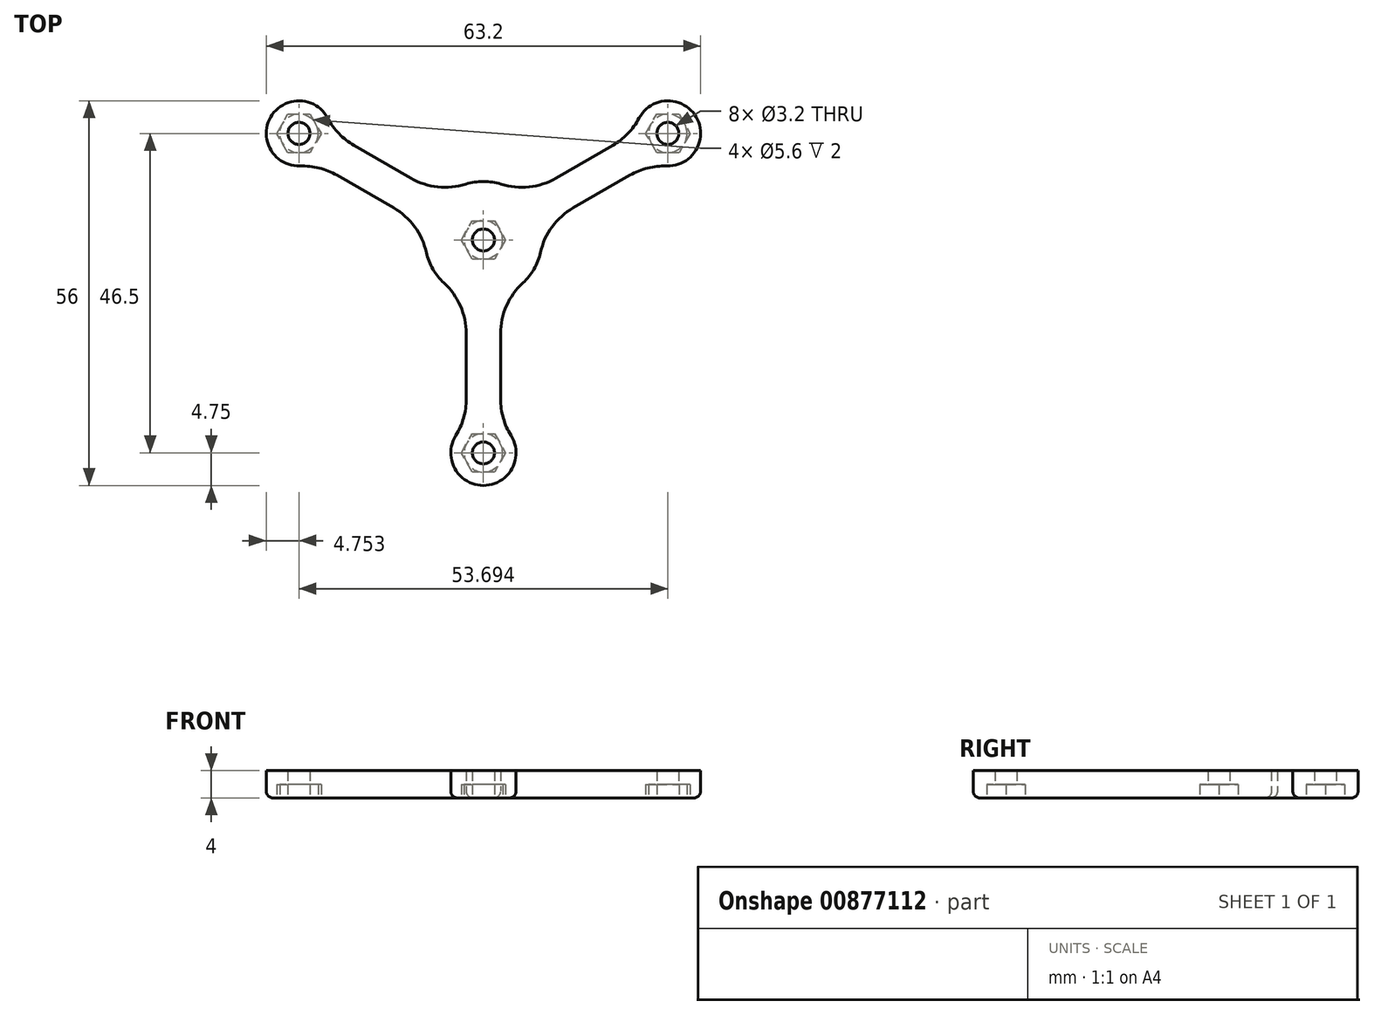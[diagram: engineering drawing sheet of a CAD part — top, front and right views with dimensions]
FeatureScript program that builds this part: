
annotation { "Feature Type Name" : "Feature", "Feature Type Description" : "" }
export const myFeature = defineFeature(function(context is Context, id is Id, definition is map)
    precondition{}
    {
        {
            var Q0;
            Q0=qCreatedBy(makeId("Top.planeOp"),FACE);
            var sketch = newSketch(context, id + "F0", { "sketchPlane" : qUnion([Q0])});
            skPoint(sketch, "E0.center", {"position": v(0, 0) * mm});
            skCircle(sketch, "E1", {"center": v(0, -31) * mm, "radius": 1.6 * mm});
            skCircle(sketch, "E2.cCircle", {"center": v(0, -31) * mm, "radius": 2.8 * mm});
            skLineSegment(sketch, "E2.0", {"start": v(3.23, -31) * mm, "end": v(1.62, -33.8) * mm});
            skLineSegment(sketch, "E2.1", {"start": v(1.62, -33.8) * mm, "end": v(-1.62, -33.8) * mm});
            skLineSegment(sketch, "E2.2", {"start": v(-1.62, -33.8) * mm, "end": v(-3.23, -31) * mm});
            skLineSegment(sketch, "E2.3", {"start": v(-3.23, -31) * mm, "end": v(-1.62, -28.2) * mm});
            skLineSegment(sketch, "E2.4", {"start": v(-1.62, -28.2) * mm, "end": v(1.62, -28.2) * mm});
            skLineSegment(sketch, "E2.5", {"start": v(1.62, -28.2) * mm, "end": v(3.23, -31) * mm});
            skPoint(sketch, "E2.0.midPoint", {"position": v(2.42, -32.4) * mm});
            skPoint(sketch, "E3.0.1.1", {"position": v(2.42, -1.4) * mm});
            skLineSegment(sketch, "E3.0.1.2", {"start": v(-1.62, -2.8) * mm, "end": v(-3.23, 0) * mm});
            skCircle(sketch, "E3.0.1.3", {"center": v(0, 0) * mm, "radius": 2.8 * mm});
            skLineSegment(sketch, "E3.0.1.4", {"start": v(1.62, -2.8) * mm, "end": v(-1.62, -2.8) * mm});
            skLineSegment(sketch, "E3.0.1.5", {"start": v(-1.62, 2.8) * mm, "end": v(1.62, 2.8) * mm});
            skLineSegment(sketch, "E3.0.1.6", {"start": v(3.23, 0) * mm, "end": v(1.62, -2.8) * mm});
            skLineSegment(sketch, "E3.0.1.7", {"start": v(1.62, 2.8) * mm, "end": v(3.23, 0) * mm});
            skLineSegment(sketch, "E3.0.1.8", {"start": v(-3.23, 0) * mm, "end": v(-1.62, 2.8) * mm});
            skCircle(sketch, "E3.0.1.9", {"center": v(0, 0) * mm, "radius": 1.6 * mm});
            skLineSegment(sketch, "E3.direction1", {"start": v(-1.62, -33.8) * mm, "end": v(2.23, -33.8) * mm, "construction": true});
            skLineSegment(sketch, "E3.direction2", {"start": v(-1.62, -33.8) * mm, "end": v(-1.62, -2.8) * mm, "construction": true});
            skLineSegment(sketch, "E4", {"start": v(-2.5, -8.12) * mm, "end": v(-2.5, -8.12) * mm});
            skLineSegment(sketch, "E5", {"start": v(2.5, -13.64) * mm, "end": v(2.5, -23.17) * mm});
            skArc(sketch, "E6", {"start": v(-5.79, 6.23) * mm, "mid": v(-5.84, 6.18) * mm, "end": v(-5.9, 6.13) * mm});
            skArc(sketch, "E7", {"start": v(-4.03, -28.48) * mm, "mid": v(0, -35.75) * mm, "end": v(4.03, -28.48) * mm});
            skLineSegment(sketch, "E8", {"start": v(-2.5, -13.64) * mm, "end": v(-2.5, -23.17) * mm});
            skArc(sketch, "E9", {"start": v(-8.3, -1.84) * mm, "mid": v(-7.36, -4.25) * mm, "end": v(-5.74, -6.27) * mm});
            skPoint(sketch, "E10.visualSharp", {"position": v(-2.5, -26.96) * mm});
            skArc(sketch, "E10.filletArc", {"start": v(-4.03, -28.48) * mm, "mid": v(-2.89, -25.93) * mm, "end": v(-2.5, -23.17) * mm});
            skPoint(sketch, "E11.visualSharp", {"position": v(2.5, -26.96) * mm});
            skArc(sketch, "E11.filletArc", {"start": v(2.5, -23.17) * mm, "mid": v(2.89, -25.93) * mm, "end": v(4.03, -28.48) * mm});
            skLineSegment(sketch, "E12.1.0", {"start": v(10.56, 8.98) * mm, "end": v(18.82, 13.75) * mm});
            skPoint(sketch, "E12.1.1", {"position": v(26.85, 18.3) * mm});
            skLineSegment(sketch, "E12.1.2", {"start": v(13.06, 4.65) * mm, "end": v(21.32, 9.42) * mm});
            skPoint(sketch, "E12.1.3", {"position": v(22.1, 15.65) * mm});
            skArc(sketch, "E12.1.4", {"start": v(26.68, 10.75) * mm, "mid": v(23.9, 10.46) * mm, "end": v(21.32, 9.42) * mm});
            skCircle(sketch, "E12.1.5", {"center": v(26.85, 15.5) * mm, "radius": 2.8 * mm});
            skCircle(sketch, "E12.1.6", {"center": v(26.85, 15.5) * mm, "radius": 1.6 * mm});
            skArc(sketch, "E12.1.7", {"start": v(26.68, 10.75) * mm, "mid": v(30.96, 17.87) * mm, "end": v(22.65, 17.73) * mm});
            skArc(sketch, "E12.1.8", {"start": v(18.82, 13.75) * mm, "mid": v(21.01, 15.47) * mm, "end": v(22.65, 17.73) * mm});
            skPoint(sketch, "E12.1.9", {"position": v(24.6, 11.32) * mm});
            skLineSegment(sketch, "E12.1.10", {"start": v(25.23, 12.7) * mm, "end": v(23.61, 15.5) * mm});
            skLineSegment(sketch, "E12.1.11", {"start": v(30.08, 15.5) * mm, "end": v(28.46, 12.7) * mm});
            skLineSegment(sketch, "E12.1.12", {"start": v(28.46, 12.7) * mm, "end": v(25.23, 12.7) * mm});
            skLineSegment(sketch, "E12.1.13", {"start": v(23.61, 15.5) * mm, "end": v(25.23, 18.3) * mm});
            skLineSegment(sketch, "E12.1.14", {"start": v(25.23, 18.3) * mm, "end": v(28.46, 18.3) * mm});
            skLineSegment(sketch, "E12.1.15", {"start": v(28.46, 18.3) * mm, "end": v(30.08, 15.5) * mm});
            skLineSegment(sketch, "E12.2.0", {"start": v(-13.06, 4.65) * mm, "end": v(-21.32, 9.42) * mm});
            skPoint(sketch, "E12.2.1", {"position": v(-29.27, 14.1) * mm});
            skLineSegment(sketch, "E12.2.2", {"start": v(-10.56, 8.98) * mm, "end": v(-18.82, 13.75) * mm});
            skPoint(sketch, "E12.2.3", {"position": v(-24.6, 11.32) * mm});
            skArc(sketch, "E12.2.4", {"start": v(-22.65, 17.73) * mm, "mid": v(-21.01, 15.47) * mm, "end": v(-18.82, 13.75) * mm});
            skCircle(sketch, "E12.2.5", {"center": v(-26.85, 15.5) * mm, "radius": 2.8 * mm});
            skCircle(sketch, "E12.2.6", {"center": v(-26.85, 15.5) * mm, "radius": 1.6 * mm});
            skArc(sketch, "E12.2.7", {"start": v(-22.65, 17.73) * mm, "mid": v(-30.96, 17.87) * mm, "end": v(-26.68, 10.75) * mm});
            skArc(sketch, "E12.2.8", {"start": v(-21.32, 9.42) * mm, "mid": v(-23.9, 10.46) * mm, "end": v(-26.68, 10.75) * mm});
            skPoint(sketch, "E12.2.9", {"position": v(-22.1, 15.65) * mm});
            skLineSegment(sketch, "E12.2.10", {"start": v(-23.61, 15.5) * mm, "end": v(-25.23, 12.7) * mm});
            skLineSegment(sketch, "E12.2.11", {"start": v(-28.46, 18.3) * mm, "end": v(-25.23, 18.3) * mm});
            skLineSegment(sketch, "E12.2.12", {"start": v(-25.23, 18.3) * mm, "end": v(-23.61, 15.5) * mm});
            skLineSegment(sketch, "E12.2.13", {"start": v(-25.23, 12.7) * mm, "end": v(-28.46, 12.7) * mm});
            skLineSegment(sketch, "E12.2.14", {"start": v(-28.46, 12.7) * mm, "end": v(-30.08, 15.5) * mm});
            skLineSegment(sketch, "E12.2.15", {"start": v(-30.08, 15.5) * mm, "end": v(-28.46, 18.3) * mm});
            skArc(sketch, "E13.trimOffspring", {"start": v(2.56, 8.1) * mm, "mid": v(0, 8.5) * mm, "end": v(-2.56, 8.1) * mm});
            skArc(sketch, "E14.trimOffspring", {"start": v(5.74, -6.27) * mm, "mid": v(7.36, -4.25) * mm, "end": v(8.3, -1.84) * mm});
            skPoint(sketch, "E15.visualSharp", {"position": v(-5.79, 6.23) * mm});
            skArc(sketch, "E15.filletArc", {"start": v(-10.56, 8.98) * mm, "mid": v(-6.65, 7.7) * mm, "end": v(-2.56, 8.1) * mm});
            skPoint(sketch, "E16.visualSharp", {"position": v(5.79, 6.23) * mm});
            skArc(sketch, "E16.filletArc", {"start": v(2.56, 8.1) * mm, "mid": v(6.65, 7.7) * mm, "end": v(10.56, 8.98) * mm});
            skPoint(sketch, "E17.visualSharp", {"position": v(8.29, 1.9) * mm});
            skArc(sketch, "E17.filletArc", {"start": v(13.06, 4.65) * mm, "mid": v(10, 1.9) * mm, "end": v(8.3, -1.84) * mm});
            skPoint(sketch, "E18.visualSharp", {"position": v(-8.29, 1.9) * mm});
            skArc(sketch, "E18.filletArc", {"start": v(-8.3, -1.84) * mm, "mid": v(-10, 1.9) * mm, "end": v(-13.06, 4.65) * mm});
            skPoint(sketch, "E19.visualSharp", {"position": v(-2.5, -8.12) * mm});
            skArc(sketch, "E19.filletArc", {"start": v(-2.5, -13.64) * mm, "mid": v(-3.35, -9.61) * mm, "end": v(-5.74, -6.27) * mm});
            skPoint(sketch, "E20.visualSharp", {"position": v(2.5, -8.12) * mm});
            skArc(sketch, "E20.filletArc", {"start": v(5.74, -6.27) * mm, "mid": v(3.35, -9.61) * mm, "end": v(2.5, -13.64) * mm});
            skCircle(sketch, "E21", {"center": v(-26.85, 15.5) * mm, "radius": 17 * mm, "construction": true});
            skCircle(sketch, "E22", {"center": v(26.85, 15.5) * mm, "radius": 17 * mm, "construction": true});
            skCircle(sketch, "E23", {"center": v(0, 0) * mm, "radius": 17 * mm, "construction": true});
            skCircle(sketch, "E24", {"center": v(0, -31) * mm, "radius": 17 * mm, "construction": true});
            skSolve(sketch);
        }
        {
            var Q0;
            {var subQ0=sQuery(id+"F0.wireOp",EDGE,"E12.2.11");var subQ1=sQuery(id+"F0.wireOp",EDGE,"E12.2.5");var subQ2=makeQuery(id+"F0.imprint","INTERSECT",VERTEX,{"derivedFrom":[subQ1,subQ0]});Q0=makeQuery(id+"F0.imprint","IMPRINT",FACE,{"disambiguationData":[TD([[makeQuery(id+"F0.imprint","IMPRINT",EDGE,{"disambiguationData":[TD([[subQ2,-1.0]])],"derivedFrom":subQ1}),-1.0]])]});}
            var Q1;
            {var subQ0=sQuery(id+"F0.wireOp",EDGE,"E12.2.15");var subQ1=sQuery(id+"F0.wireOp",EDGE,"E12.2.5");var subQ2=makeQuery(id+"F0.imprint","INTERSECT",VERTEX,{"derivedFrom":[subQ1,subQ0]});Q1=makeQuery(id+"F0.imprint","IMPRINT",FACE,{"disambiguationData":[TD([[makeQuery(id+"F0.imprint","IMPRINT",EDGE,{"disambiguationData":[TD([[subQ2,-1.0]])],"derivedFrom":subQ1}),-1.0]])]});}
            var Q2;
            {var subQ0=sQuery(id+"F0.wireOp",EDGE,"E12.2.13");var subQ1=sQuery(id+"F0.wireOp",EDGE,"E12.2.5");var subQ2=makeQuery(id+"F0.imprint","INTERSECT",VERTEX,{"derivedFrom":[subQ1,subQ0]});Q2=makeQuery(id+"F0.imprint","IMPRINT",FACE,{"disambiguationData":[TD([[makeQuery(id+"F0.imprint","IMPRINT",EDGE,{"disambiguationData":[TD([[subQ2,1.0]])],"derivedFrom":subQ1}),-1.0]])]});}
            var Q3;
            Q3=makeQuery(id+"F0.imprint","IMPRINT",FACE,{"disambiguationData":[TD([[makeQuery(id+"F0.imprint","IMPRINT",EDGE,{"derivedFrom":sQuery(id+"F0.wireOp",EDGE,"E12.2.6")}),-1.0]])]});
            var Q4;
            {var subQ0=sQuery(id+"F0.wireOp",EDGE,"E12.2.12");var subQ1=sQuery(id+"F0.wireOp",EDGE,"E12.2.5");var subQ2=makeQuery(id+"F0.imprint","INTERSECT",VERTEX,{"derivedFrom":[subQ1,subQ0]});Q4=makeQuery(id+"F0.imprint","IMPRINT",FACE,{"disambiguationData":[TD([[makeQuery(id+"F0.imprint","IMPRINT",EDGE,{"disambiguationData":[TD([[subQ2,-1.0]])],"derivedFrom":subQ1}),-1.0]])]});}
            var Q5;
            {var subQ0=sQuery(id+"F0.wireOp",EDGE,"E12.2.10");var subQ1=sQuery(id+"F0.wireOp",EDGE,"E12.2.5");var subQ2=makeQuery(id+"F0.imprint","INTERSECT",VERTEX,{"derivedFrom":[subQ1,subQ0]});Q5=makeQuery(id+"F0.imprint","IMPRINT",FACE,{"disambiguationData":[TD([[makeQuery(id+"F0.imprint","IMPRINT",EDGE,{"disambiguationData":[TD([[subQ2,-1.0]])],"derivedFrom":subQ1}),-1.0]])]});}
            var Q6;
            {var subQ0=sQuery(id+"F0.wireOp",EDGE,"E12.2.10");var subQ1=sQuery(id+"F0.wireOp",EDGE,"E12.2.5");var subQ2=makeQuery(id+"F0.imprint","INTERSECT",VERTEX,{"derivedFrom":[subQ1,subQ0]});Q6=makeQuery(id+"F0.imprint","IMPRINT",FACE,{"disambiguationData":[TD([[makeQuery(id+"F0.imprint","IMPRINT",EDGE,{"disambiguationData":[TD([[subQ2,1.0]])],"derivedFrom":subQ1}),-1.0]])]});}
            var Q7;
            {var subQ0=sQuery(id+"F0.wireOp",EDGE,"E3.0.1.5");var subQ1=sQuery(id+"F0.wireOp",EDGE,"E3.0.1.3");var subQ2=makeQuery(id+"F0.imprint","INTERSECT",VERTEX,{"derivedFrom":[subQ1,subQ0]});Q7=makeQuery(id+"F0.imprint","IMPRINT",FACE,{"disambiguationData":[TD([[makeQuery(id+"F0.imprint","IMPRINT",EDGE,{"disambiguationData":[TD([[subQ2,-1.0]])],"derivedFrom":subQ1}),-1.0]])]});}
            var Q8;
            Q8=makeQuery(id+"F0.imprint","IMPRINT",FACE,{"disambiguationData":[TD([[makeQuery(id+"F0.imprint","IMPRINT",EDGE,{"derivedFrom":sQuery(id+"F0.wireOp",EDGE,"E3.0.1.9")}),-1.0]])]});
            var Q9;
            {var subQ0=sQuery(id+"F0.wireOp",EDGE,"E3.0.1.5");var subQ1=sQuery(id+"F0.wireOp",EDGE,"E3.0.1.3");var subQ2=makeQuery(id+"F0.imprint","INTERSECT",VERTEX,{"derivedFrom":[subQ1,subQ0]});Q9=makeQuery(id+"F0.imprint","IMPRINT",FACE,{"disambiguationData":[TD([[makeQuery(id+"F0.imprint","IMPRINT",EDGE,{"disambiguationData":[TD([[subQ2,1.0]])],"derivedFrom":subQ1}),-1.0]])]});}
            var Q10;
            {var subQ0=sQuery(id+"F0.wireOp",EDGE,"E3.0.1.7");var subQ1=sQuery(id+"F0.wireOp",EDGE,"E3.0.1.3");var subQ2=makeQuery(id+"F0.imprint","INTERSECT",VERTEX,{"derivedFrom":[subQ1,subQ0]});Q10=makeQuery(id+"F0.imprint","IMPRINT",FACE,{"disambiguationData":[TD([[makeQuery(id+"F0.imprint","IMPRINT",EDGE,{"disambiguationData":[TD([[subQ2,1.0]])],"derivedFrom":subQ1}),-1.0]])]});}
            var Q11;
            {var subQ0=sQuery(id+"F0.wireOp",EDGE,"E3.0.1.4");var subQ1=sQuery(id+"F0.wireOp",EDGE,"E3.0.1.3");var subQ2=makeQuery(id+"F0.imprint","INTERSECT",VERTEX,{"derivedFrom":[subQ1,subQ0]});Q11=makeQuery(id+"F0.imprint","IMPRINT",FACE,{"disambiguationData":[TD([[makeQuery(id+"F0.imprint","IMPRINT",EDGE,{"disambiguationData":[TD([[subQ2,-1.0]])],"derivedFrom":subQ1}),-1.0]])]});}
            var Q12;
            {var subQ0=sQuery(id+"F0.wireOp",EDGE,"E3.0.1.4");var subQ1=sQuery(id+"F0.wireOp",EDGE,"E3.0.1.2");var subQ2=makeQuery(id+"F0.imprint","INTERSECT",VERTEX,{"derivedFrom":[subQ1,subQ0]});Q12=makeQuery(id+"F0.imprint","IMPRINT",FACE,{"disambiguationData":[TD([[makeQuery(id+"F0.imprint","IMPRINT",EDGE,{"disambiguationData":[TD([[subQ2,-1.0]])],"derivedFrom":subQ1}),-1.0]])]});}
            var Q13;
            {var subQ0=sQuery(id+"F0.wireOp",EDGE,"E3.0.1.8");var subQ1=sQuery(id+"F0.wireOp",EDGE,"E3.0.1.2");var subQ2=makeQuery(id+"F0.imprint","INTERSECT",VERTEX,{"derivedFrom":[subQ1,subQ0]});Q13=makeQuery(id+"F0.imprint","IMPRINT",FACE,{"disambiguationData":[TD([[makeQuery(id+"F0.imprint","IMPRINT",EDGE,{"disambiguationData":[TD([[subQ2,1.0]])],"derivedFrom":subQ1}),-1.0]])]});}
            var Q14;
            Q14=makeQuery(id+"F0.imprint","IMPRINT",FACE,{"disambiguationData":[TD([[makeQuery(id+"F0.imprint","IMPRINT",EDGE,{"derivedFrom":sQuery(id+"F0.wireOp",EDGE,"E5")}),-1.0]])]});
            var Q15;
            {var subQ0=sQuery(id+"F0.wireOp",EDGE,"E12.1.13");var subQ1=sQuery(id+"F0.wireOp",EDGE,"E12.1.5");var subQ2=makeQuery(id+"F0.imprint","INTERSECT",VERTEX,{"derivedFrom":[subQ1,subQ0]});Q15=makeQuery(id+"F0.imprint","IMPRINT",FACE,{"disambiguationData":[TD([[makeQuery(id+"F0.imprint","IMPRINT",EDGE,{"disambiguationData":[TD([[subQ2,1.0]])],"derivedFrom":subQ1}),-1.0]])]});}
            var Q16;
            {var subQ0=sQuery(id+"F0.wireOp",EDGE,"E12.1.10");var subQ1=sQuery(id+"F0.wireOp",EDGE,"E12.1.5");var subQ2=makeQuery(id+"F0.imprint","INTERSECT",VERTEX,{"derivedFrom":[subQ1,subQ0]});Q16=makeQuery(id+"F0.imprint","IMPRINT",FACE,{"disambiguationData":[TD([[makeQuery(id+"F0.imprint","IMPRINT",EDGE,{"disambiguationData":[TD([[subQ2,1.0]])],"derivedFrom":subQ1}),-1.0]])]});}
            var Q17;
            {var subQ0=sQuery(id+"F0.wireOp",EDGE,"E12.1.10");var subQ1=sQuery(id+"F0.wireOp",EDGE,"E12.1.5");var subQ2=makeQuery(id+"F0.imprint","INTERSECT",VERTEX,{"derivedFrom":[subQ1,subQ0]});Q17=makeQuery(id+"F0.imprint","IMPRINT",FACE,{"disambiguationData":[TD([[makeQuery(id+"F0.imprint","IMPRINT",EDGE,{"disambiguationData":[TD([[subQ2,-1.0]])],"derivedFrom":subQ1}),-1.0]])]});}
            var Q18;
            {var subQ0=sQuery(id+"F0.wireOp",EDGE,"E12.1.12");var subQ1=sQuery(id+"F0.wireOp",EDGE,"E12.1.5");var subQ2=makeQuery(id+"F0.imprint","INTERSECT",VERTEX,{"derivedFrom":[subQ1,subQ0]});Q18=makeQuery(id+"F0.imprint","IMPRINT",FACE,{"disambiguationData":[TD([[makeQuery(id+"F0.imprint","IMPRINT",EDGE,{"disambiguationData":[TD([[subQ2,-1.0]])],"derivedFrom":subQ1}),-1.0]])]});}
            var Q19;
            {var subQ0=sQuery(id+"F0.wireOp",EDGE,"E12.1.11");var subQ1=sQuery(id+"F0.wireOp",EDGE,"E12.1.5");var subQ2=makeQuery(id+"F0.imprint","INTERSECT",VERTEX,{"derivedFrom":[subQ1,subQ0]});Q19=makeQuery(id+"F0.imprint","IMPRINT",FACE,{"disambiguationData":[TD([[makeQuery(id+"F0.imprint","IMPRINT",EDGE,{"disambiguationData":[TD([[subQ2,-1.0]])],"derivedFrom":subQ1}),-1.0]])]});}
            var Q20;
            {var subQ0=sQuery(id+"F0.wireOp",EDGE,"E12.1.15");var subQ1=sQuery(id+"F0.wireOp",EDGE,"E12.1.5");var subQ2=makeQuery(id+"F0.imprint","INTERSECT",VERTEX,{"derivedFrom":[subQ1,subQ0]});Q20=makeQuery(id+"F0.imprint","IMPRINT",FACE,{"disambiguationData":[TD([[makeQuery(id+"F0.imprint","IMPRINT",EDGE,{"disambiguationData":[TD([[subQ2,-1.0]])],"derivedFrom":subQ1}),-1.0]])]});}
            var Q21;
            Q21=makeQuery(id+"F0.imprint","IMPRINT",FACE,{"disambiguationData":[TD([[makeQuery(id+"F0.imprint","IMPRINT",EDGE,{"derivedFrom":sQuery(id+"F0.wireOp",EDGE,"E12.1.6")}),-1.0]])]});
            var Q22;
            {var subQ0=sQuery(id+"F0.wireOp",EDGE,"E2.3");var subQ1=sQuery(id+"F0.wireOp",EDGE,"E2.cCircle");var subQ2=makeQuery(id+"F0.imprint","INTERSECT",VERTEX,{"derivedFrom":[subQ1,subQ0]});Q22=makeQuery(id+"F0.imprint","IMPRINT",FACE,{"disambiguationData":[TD([[makeQuery(id+"F0.imprint","IMPRINT",EDGE,{"disambiguationData":[TD([[subQ2,-1.0]])],"derivedFrom":subQ1}),-1.0]])]});}
            var Q23;
            {var subQ0=sQuery(id+"F0.wireOp",EDGE,"E2.4");var subQ1=sQuery(id+"F0.wireOp",EDGE,"E2.cCircle");var subQ2=makeQuery(id+"F0.imprint","INTERSECT",VERTEX,{"derivedFrom":[subQ1,subQ0]});Q23=makeQuery(id+"F0.imprint","IMPRINT",FACE,{"disambiguationData":[TD([[makeQuery(id+"F0.imprint","IMPRINT",EDGE,{"disambiguationData":[TD([[subQ2,-1.0]])],"derivedFrom":subQ1}),-1.0]])]});}
            var Q24;
            Q24=makeQuery(id+"F0.imprint","IMPRINT",FACE,{"disambiguationData":[TD([[makeQuery(id+"F0.imprint","IMPRINT",EDGE,{"derivedFrom":sQuery(id+"F0.wireOp",EDGE,"E1")}),-1.0]])]});
            var Q25;
            {var subQ0=sQuery(id+"F0.wireOp",EDGE,"E2.4");var subQ1=sQuery(id+"F0.wireOp",EDGE,"E2.cCircle");var subQ2=makeQuery(id+"F0.imprint","INTERSECT",VERTEX,{"derivedFrom":[subQ1,subQ0]});Q25=makeQuery(id+"F0.imprint","IMPRINT",FACE,{"disambiguationData":[TD([[makeQuery(id+"F0.imprint","IMPRINT",EDGE,{"disambiguationData":[TD([[subQ2,1.0]])],"derivedFrom":subQ1}),-1.0]])]});}
            var Q26;
            {var subQ0=sQuery(id+"F0.wireOp",EDGE,"E2.5");var subQ1=sQuery(id+"F0.wireOp",EDGE,"E2.cCircle");var subQ2=makeQuery(id+"F0.imprint","INTERSECT",VERTEX,{"derivedFrom":[subQ1,subQ0]});Q26=makeQuery(id+"F0.imprint","IMPRINT",FACE,{"disambiguationData":[TD([[makeQuery(id+"F0.imprint","IMPRINT",EDGE,{"disambiguationData":[TD([[subQ2,1.0]])],"derivedFrom":subQ1}),-1.0]])]});}
            var Q27;
            {var subQ0=sQuery(id+"F0.wireOp",EDGE,"E2.1");var subQ1=sQuery(id+"F0.wireOp",EDGE,"E2.cCircle");var subQ2=makeQuery(id+"F0.imprint","INTERSECT",VERTEX,{"derivedFrom":[subQ1,subQ0]});Q27=makeQuery(id+"F0.imprint","IMPRINT",FACE,{"disambiguationData":[TD([[makeQuery(id+"F0.imprint","IMPRINT",EDGE,{"disambiguationData":[TD([[subQ2,-1.0]])],"derivedFrom":subQ1}),-1.0]])]});}
            var Q28;
            {var subQ0=sQuery(id+"F0.wireOp",EDGE,"E2.2");var subQ1=sQuery(id+"F0.wireOp",EDGE,"E2.cCircle");var subQ2=makeQuery(id+"F0.imprint","INTERSECT",VERTEX,{"derivedFrom":[subQ1,subQ0]});Q28=makeQuery(id+"F0.imprint","IMPRINT",FACE,{"disambiguationData":[TD([[makeQuery(id+"F0.imprint","IMPRINT",EDGE,{"disambiguationData":[TD([[subQ2,-1.0]])],"derivedFrom":subQ1}),-1.0]])]});}
            extrude(context, id + "F1", {"entities" : qUnion([Q0, Q1, Q2, Q3, Q4, Q5, Q6, Q7, Q8, Q9, Q10, Q11, Q12, Q13, Q14, Q15, Q16, Q17, Q18, Q19, Q20, Q21, Q22, Q23, Q24, Q25, Q26, Q27, Q28]), "depth" : 4 * mm, "offsetDistance" : 25 * mm});
        }
        {
            var Q0;
            {var subQ0=sQuery(id+"F0.wireOp",EDGE,"E12.2.13");var subQ1=sQuery(id+"F0.wireOp",EDGE,"E12.2.5");var subQ2=makeQuery(id+"F0.imprint","INTERSECT",VERTEX,{"derivedFrom":[subQ1,subQ0]});Q0=makeQuery(id+"F0.imprint","IMPRINT",FACE,{"disambiguationData":[TD([[makeQuery(id+"F0.imprint","IMPRINT",EDGE,{"disambiguationData":[TD([[subQ2,1.0]])],"derivedFrom":subQ1}),-1.0]])]});}
            var Q1;
            Q1=makeQuery(id+"F0.imprint","IMPRINT",FACE,{"disambiguationData":[TD([[makeQuery(id+"F0.imprint","IMPRINT",EDGE,{"derivedFrom":sQuery(id+"F0.wireOp",EDGE,"E12.2.6")}),-1.0]])]});
            var Q2;
            {var subQ0=sQuery(id+"F0.wireOp",EDGE,"E12.2.15");var subQ1=sQuery(id+"F0.wireOp",EDGE,"E12.2.5");var subQ2=makeQuery(id+"F0.imprint","INTERSECT",VERTEX,{"derivedFrom":[subQ1,subQ0]});Q2=makeQuery(id+"F0.imprint","IMPRINT",FACE,{"disambiguationData":[TD([[makeQuery(id+"F0.imprint","IMPRINT",EDGE,{"disambiguationData":[TD([[subQ2,-1.0]])],"derivedFrom":subQ1}),-1.0]])]});}
            var Q3;
            {var subQ0=sQuery(id+"F0.wireOp",EDGE,"E12.2.11");var subQ1=sQuery(id+"F0.wireOp",EDGE,"E12.2.5");var subQ2=makeQuery(id+"F0.imprint","INTERSECT",VERTEX,{"derivedFrom":[subQ1,subQ0]});Q3=makeQuery(id+"F0.imprint","IMPRINT",FACE,{"disambiguationData":[TD([[makeQuery(id+"F0.imprint","IMPRINT",EDGE,{"disambiguationData":[TD([[subQ2,-1.0]])],"derivedFrom":subQ1}),-1.0]])]});}
            var Q4;
            {var subQ0=sQuery(id+"F0.wireOp",EDGE,"E12.2.12");var subQ1=sQuery(id+"F0.wireOp",EDGE,"E12.2.5");var subQ2=makeQuery(id+"F0.imprint","INTERSECT",VERTEX,{"derivedFrom":[subQ1,subQ0]});Q4=makeQuery(id+"F0.imprint","IMPRINT",FACE,{"disambiguationData":[TD([[makeQuery(id+"F0.imprint","IMPRINT",EDGE,{"disambiguationData":[TD([[subQ2,-1.0]])],"derivedFrom":subQ1}),-1.0]])]});}
            var Q5;
            {var subQ0=sQuery(id+"F0.wireOp",EDGE,"E12.2.10");var subQ1=sQuery(id+"F0.wireOp",EDGE,"E12.2.5");var subQ2=makeQuery(id+"F0.imprint","INTERSECT",VERTEX,{"derivedFrom":[subQ1,subQ0]});Q5=makeQuery(id+"F0.imprint","IMPRINT",FACE,{"disambiguationData":[TD([[makeQuery(id+"F0.imprint","IMPRINT",EDGE,{"disambiguationData":[TD([[subQ2,-1.0]])],"derivedFrom":subQ1}),-1.0]])]});}
            var Q6;
            {var subQ0=sQuery(id+"F0.wireOp",EDGE,"E12.2.10");var subQ1=sQuery(id+"F0.wireOp",EDGE,"E12.2.5");var subQ2=makeQuery(id+"F0.imprint","INTERSECT",VERTEX,{"derivedFrom":[subQ1,subQ0]});Q6=makeQuery(id+"F0.imprint","IMPRINT",FACE,{"disambiguationData":[TD([[makeQuery(id+"F0.imprint","IMPRINT",EDGE,{"disambiguationData":[TD([[subQ2,1.0]])],"derivedFrom":subQ1}),-1.0]])]});}
            var Q7;
            {var subQ0=sQuery(id+"F0.wireOp",EDGE,"E3.0.1.8");var subQ1=sQuery(id+"F0.wireOp",EDGE,"E3.0.1.2");var subQ2=makeQuery(id+"F0.imprint","INTERSECT",VERTEX,{"derivedFrom":[subQ1,subQ0]});Q7=makeQuery(id+"F0.imprint","IMPRINT",FACE,{"disambiguationData":[TD([[makeQuery(id+"F0.imprint","IMPRINT",EDGE,{"disambiguationData":[TD([[subQ2,1.0]])],"derivedFrom":subQ1}),-1.0]])]});}
            var Q8;
            {var subQ0=sQuery(id+"F0.wireOp",EDGE,"E3.0.1.4");var subQ1=sQuery(id+"F0.wireOp",EDGE,"E3.0.1.2");var subQ2=makeQuery(id+"F0.imprint","INTERSECT",VERTEX,{"derivedFrom":[subQ1,subQ0]});Q8=makeQuery(id+"F0.imprint","IMPRINT",FACE,{"disambiguationData":[TD([[makeQuery(id+"F0.imprint","IMPRINT",EDGE,{"disambiguationData":[TD([[subQ2,-1.0]])],"derivedFrom":subQ1}),-1.0]])]});}
            var Q9;
            {var subQ0=sQuery(id+"F0.wireOp",EDGE,"E3.0.1.4");var subQ1=sQuery(id+"F0.wireOp",EDGE,"E3.0.1.3");var subQ2=makeQuery(id+"F0.imprint","INTERSECT",VERTEX,{"derivedFrom":[subQ1,subQ0]});Q9=makeQuery(id+"F0.imprint","IMPRINT",FACE,{"disambiguationData":[TD([[makeQuery(id+"F0.imprint","IMPRINT",EDGE,{"disambiguationData":[TD([[subQ2,-1.0]])],"derivedFrom":subQ1}),-1.0]])]});}
            var Q10;
            {var subQ0=sQuery(id+"F0.wireOp",EDGE,"E3.0.1.7");var subQ1=sQuery(id+"F0.wireOp",EDGE,"E3.0.1.3");var subQ2=makeQuery(id+"F0.imprint","INTERSECT",VERTEX,{"derivedFrom":[subQ1,subQ0]});Q10=makeQuery(id+"F0.imprint","IMPRINT",FACE,{"disambiguationData":[TD([[makeQuery(id+"F0.imprint","IMPRINT",EDGE,{"disambiguationData":[TD([[subQ2,1.0]])],"derivedFrom":subQ1}),-1.0]])]});}
            var Q11;
            {var subQ0=sQuery(id+"F0.wireOp",EDGE,"E3.0.1.5");var subQ1=sQuery(id+"F0.wireOp",EDGE,"E3.0.1.3");var subQ2=makeQuery(id+"F0.imprint","INTERSECT",VERTEX,{"derivedFrom":[subQ1,subQ0]});Q11=makeQuery(id+"F0.imprint","IMPRINT",FACE,{"disambiguationData":[TD([[makeQuery(id+"F0.imprint","IMPRINT",EDGE,{"disambiguationData":[TD([[subQ2,1.0]])],"derivedFrom":subQ1}),-1.0]])]});}
            var Q12;
            {var subQ0=sQuery(id+"F0.wireOp",EDGE,"E3.0.1.5");var subQ1=sQuery(id+"F0.wireOp",EDGE,"E3.0.1.3");var subQ2=makeQuery(id+"F0.imprint","INTERSECT",VERTEX,{"derivedFrom":[subQ1,subQ0]});Q12=makeQuery(id+"F0.imprint","IMPRINT",FACE,{"disambiguationData":[TD([[makeQuery(id+"F0.imprint","IMPRINT",EDGE,{"disambiguationData":[TD([[subQ2,-1.0]])],"derivedFrom":subQ1}),-1.0]])]});}
            var Q13;
            Q13=makeQuery(id+"F0.imprint","IMPRINT",FACE,{"disambiguationData":[TD([[makeQuery(id+"F0.imprint","IMPRINT",EDGE,{"derivedFrom":sQuery(id+"F0.wireOp",EDGE,"E3.0.1.9")}),-1.0]])]});
            var Q14;
            Q14=makeQuery(id+"F0.imprint","IMPRINT",FACE,{"disambiguationData":[TD([[makeQuery(id+"F0.imprint","IMPRINT",EDGE,{"derivedFrom":sQuery(id+"F0.wireOp",EDGE,"E12.1.6")}),-1.0]])]});
            var Q15;
            {var subQ0=sQuery(id+"F0.wireOp",EDGE,"E12.1.10");var subQ1=sQuery(id+"F0.wireOp",EDGE,"E12.1.5");var subQ2=makeQuery(id+"F0.imprint","INTERSECT",VERTEX,{"derivedFrom":[subQ1,subQ0]});Q15=makeQuery(id+"F0.imprint","IMPRINT",FACE,{"disambiguationData":[TD([[makeQuery(id+"F0.imprint","IMPRINT",EDGE,{"disambiguationData":[TD([[subQ2,1.0]])],"derivedFrom":subQ1}),-1.0]])]});}
            var Q16;
            {var subQ0=sQuery(id+"F0.wireOp",EDGE,"E12.1.10");var subQ1=sQuery(id+"F0.wireOp",EDGE,"E12.1.5");var subQ2=makeQuery(id+"F0.imprint","INTERSECT",VERTEX,{"derivedFrom":[subQ1,subQ0]});Q16=makeQuery(id+"F0.imprint","IMPRINT",FACE,{"disambiguationData":[TD([[makeQuery(id+"F0.imprint","IMPRINT",EDGE,{"disambiguationData":[TD([[subQ2,-1.0]])],"derivedFrom":subQ1}),-1.0]])]});}
            var Q17;
            {var subQ0=sQuery(id+"F0.wireOp",EDGE,"E12.1.12");var subQ1=sQuery(id+"F0.wireOp",EDGE,"E12.1.5");var subQ2=makeQuery(id+"F0.imprint","INTERSECT",VERTEX,{"derivedFrom":[subQ1,subQ0]});Q17=makeQuery(id+"F0.imprint","IMPRINT",FACE,{"disambiguationData":[TD([[makeQuery(id+"F0.imprint","IMPRINT",EDGE,{"disambiguationData":[TD([[subQ2,-1.0]])],"derivedFrom":subQ1}),-1.0]])]});}
            var Q18;
            {var subQ0=sQuery(id+"F0.wireOp",EDGE,"E12.1.11");var subQ1=sQuery(id+"F0.wireOp",EDGE,"E12.1.5");var subQ2=makeQuery(id+"F0.imprint","INTERSECT",VERTEX,{"derivedFrom":[subQ1,subQ0]});Q18=makeQuery(id+"F0.imprint","IMPRINT",FACE,{"disambiguationData":[TD([[makeQuery(id+"F0.imprint","IMPRINT",EDGE,{"disambiguationData":[TD([[subQ2,-1.0]])],"derivedFrom":subQ1}),-1.0]])]});}
            var Q19;
            {var subQ0=sQuery(id+"F0.wireOp",EDGE,"E12.1.15");var subQ1=sQuery(id+"F0.wireOp",EDGE,"E12.1.5");var subQ2=makeQuery(id+"F0.imprint","INTERSECT",VERTEX,{"derivedFrom":[subQ1,subQ0]});Q19=makeQuery(id+"F0.imprint","IMPRINT",FACE,{"disambiguationData":[TD([[makeQuery(id+"F0.imprint","IMPRINT",EDGE,{"disambiguationData":[TD([[subQ2,-1.0]])],"derivedFrom":subQ1}),-1.0]])]});}
            var Q20;
            {var subQ0=sQuery(id+"F0.wireOp",EDGE,"E12.1.13");var subQ1=sQuery(id+"F0.wireOp",EDGE,"E12.1.5");var subQ2=makeQuery(id+"F0.imprint","INTERSECT",VERTEX,{"derivedFrom":[subQ1,subQ0]});Q20=makeQuery(id+"F0.imprint","IMPRINT",FACE,{"disambiguationData":[TD([[makeQuery(id+"F0.imprint","IMPRINT",EDGE,{"disambiguationData":[TD([[subQ2,1.0]])],"derivedFrom":subQ1}),-1.0]])]});}
            var Q21;
            Q21=makeQuery(id+"F0.imprint","IMPRINT",FACE,{"disambiguationData":[TD([[makeQuery(id+"F0.imprint","IMPRINT",EDGE,{"derivedFrom":sQuery(id+"F0.wireOp",EDGE,"E1")}),-1.0]])]});
            var Q22;
            {var subQ0=sQuery(id+"F0.wireOp",EDGE,"E2.2");var subQ1=sQuery(id+"F0.wireOp",EDGE,"E2.cCircle");var subQ2=makeQuery(id+"F0.imprint","INTERSECT",VERTEX,{"derivedFrom":[subQ1,subQ0]});Q22=makeQuery(id+"F0.imprint","IMPRINT",FACE,{"disambiguationData":[TD([[makeQuery(id+"F0.imprint","IMPRINT",EDGE,{"disambiguationData":[TD([[subQ2,-1.0]])],"derivedFrom":subQ1}),-1.0]])]});}
            var Q23;
            {var subQ0=sQuery(id+"F0.wireOp",EDGE,"E2.1");var subQ1=sQuery(id+"F0.wireOp",EDGE,"E2.cCircle");var subQ2=makeQuery(id+"F0.imprint","INTERSECT",VERTEX,{"derivedFrom":[subQ1,subQ0]});Q23=makeQuery(id+"F0.imprint","IMPRINT",FACE,{"disambiguationData":[TD([[makeQuery(id+"F0.imprint","IMPRINT",EDGE,{"disambiguationData":[TD([[subQ2,-1.0]])],"derivedFrom":subQ1}),-1.0]])]});}
            var Q24;
            {var subQ0=sQuery(id+"F0.wireOp",EDGE,"E2.5");var subQ1=sQuery(id+"F0.wireOp",EDGE,"E2.cCircle");var subQ2=makeQuery(id+"F0.imprint","INTERSECT",VERTEX,{"derivedFrom":[subQ1,subQ0]});Q24=makeQuery(id+"F0.imprint","IMPRINT",FACE,{"disambiguationData":[TD([[makeQuery(id+"F0.imprint","IMPRINT",EDGE,{"disambiguationData":[TD([[subQ2,1.0]])],"derivedFrom":subQ1}),-1.0]])]});}
            var Q25;
            {var subQ0=sQuery(id+"F0.wireOp",EDGE,"E2.4");var subQ1=sQuery(id+"F0.wireOp",EDGE,"E2.cCircle");var subQ2=makeQuery(id+"F0.imprint","INTERSECT",VERTEX,{"derivedFrom":[subQ1,subQ0]});Q25=makeQuery(id+"F0.imprint","IMPRINT",FACE,{"disambiguationData":[TD([[makeQuery(id+"F0.imprint","IMPRINT",EDGE,{"disambiguationData":[TD([[subQ2,1.0]])],"derivedFrom":subQ1}),-1.0]])]});}
            var Q26;
            {var subQ0=sQuery(id+"F0.wireOp",EDGE,"E2.4");var subQ1=sQuery(id+"F0.wireOp",EDGE,"E2.cCircle");var subQ2=makeQuery(id+"F0.imprint","INTERSECT",VERTEX,{"derivedFrom":[subQ1,subQ0]});Q26=makeQuery(id+"F0.imprint","IMPRINT",FACE,{"disambiguationData":[TD([[makeQuery(id+"F0.imprint","IMPRINT",EDGE,{"disambiguationData":[TD([[subQ2,-1.0]])],"derivedFrom":subQ1}),-1.0]])]});}
            var Q27;
            {var subQ0=sQuery(id+"F0.wireOp",EDGE,"E2.3");var subQ1=sQuery(id+"F0.wireOp",EDGE,"E2.cCircle");var subQ2=makeQuery(id+"F0.imprint","INTERSECT",VERTEX,{"derivedFrom":[subQ1,subQ0]});Q27=makeQuery(id+"F0.imprint","IMPRINT",FACE,{"disambiguationData":[TD([[makeQuery(id+"F0.imprint","IMPRINT",EDGE,{"disambiguationData":[TD([[subQ2,-1.0]])],"derivedFrom":subQ1}),-1.0]])]});}
            extrude(context, id + "F2", {"entities" : qUnion([Q0, Q1, Q2, Q3, Q4, Q5, Q6, Q7, Q8, Q9, Q10, Q11, Q12, Q13, Q14, Q15, Q16, Q17, Q18, Q19, Q20, Q21, Q22, Q23, Q24, Q25, Q26, Q27]), "operationType" : NewBodyOperationType.REMOVE, "depth" : 2 * mm, "offsetDistance" : 25 * mm});
        }
        {
            var Q0;
            Q0=makeQuery(id+"F1.opExtrude","CAP_EDGE",EDGE,{"disambiguationData":[OSD([sQuery(id+"F0.wireOp",EDGE,"E8")])],"isStart":true});
            fillet(context, id + "F3", {"entities" : qUnion([Q0]), "radius" : 1 * mm, "tangentPropagation" : true, "allowEdgeOverflow" : false});
        }
        {
            var Q0;
            Q0 = qSketchRegion(id + "F0", true);
            var Q1;
            {var subQ0=sQuery(id+"F0.wireOp",EDGE,"E12.2.15");var subQ1=sQuery(id+"F0.wireOp",EDGE,"E12.2.5");var subQ2=makeQuery(id+"F0.imprint","INTERSECT",VERTEX,{"derivedFrom":[subQ1,subQ0]});Q1=makeQuery(id+"F0.imprint","IMPRINT",FACE,{"disambiguationData":[TD([[makeQuery(id+"F0.imprint","IMPRINT",EDGE,{"disambiguationData":[TD([[subQ2,-1.0]])],"derivedFrom":subQ1}),-1.0]])]});}
            var Q2;
            Q2=makeQuery(id+"F0.imprint","IMPRINT",FACE,{"disambiguationData":[TD([[makeQuery(id+"F0.imprint","IMPRINT",EDGE,{"derivedFrom":sQuery(id+"F0.wireOp",EDGE,"E12.2.6")}),-1.0]])]});
            var Q3;
            {var subQ0=sQuery(id+"F0.wireOp",EDGE,"E12.2.13");var subQ1=sQuery(id+"F0.wireOp",EDGE,"E12.2.5");var subQ2=makeQuery(id+"F0.imprint","INTERSECT",VERTEX,{"derivedFrom":[subQ1,subQ0]});Q3=makeQuery(id+"F0.imprint","IMPRINT",FACE,{"disambiguationData":[TD([[makeQuery(id+"F0.imprint","IMPRINT",EDGE,{"disambiguationData":[TD([[subQ2,1.0]])],"derivedFrom":subQ1}),-1.0]])]});}
            var Q4;
            {var subQ0=sQuery(id+"F0.wireOp",EDGE,"E12.2.10");var subQ1=sQuery(id+"F0.wireOp",EDGE,"E12.2.5");var subQ2=makeQuery(id+"F0.imprint","INTERSECT",VERTEX,{"derivedFrom":[subQ1,subQ0]});Q4=makeQuery(id+"F0.imprint","IMPRINT",FACE,{"disambiguationData":[TD([[makeQuery(id+"F0.imprint","IMPRINT",EDGE,{"disambiguationData":[TD([[subQ2,1.0]])],"derivedFrom":subQ1}),-1.0]])]});}
            var Q5;
            {var subQ0=sQuery(id+"F0.wireOp",EDGE,"E12.2.10");var subQ1=sQuery(id+"F0.wireOp",EDGE,"E12.2.5");var subQ2=makeQuery(id+"F0.imprint","INTERSECT",VERTEX,{"derivedFrom":[subQ1,subQ0]});Q5=makeQuery(id+"F0.imprint","IMPRINT",FACE,{"disambiguationData":[TD([[makeQuery(id+"F0.imprint","IMPRINT",EDGE,{"disambiguationData":[TD([[subQ2,-1.0]])],"derivedFrom":subQ1}),-1.0]])]});}
            var Q6;
            {var subQ0=sQuery(id+"F0.wireOp",EDGE,"E12.2.12");var subQ1=sQuery(id+"F0.wireOp",EDGE,"E12.2.5");var subQ2=makeQuery(id+"F0.imprint","INTERSECT",VERTEX,{"derivedFrom":[subQ1,subQ0]});Q6=makeQuery(id+"F0.imprint","IMPRINT",FACE,{"disambiguationData":[TD([[makeQuery(id+"F0.imprint","IMPRINT",EDGE,{"disambiguationData":[TD([[subQ2,-1.0]])],"derivedFrom":subQ1}),-1.0]])]});}
            var Q7;
            {var subQ0=sQuery(id+"F0.wireOp",EDGE,"E12.2.11");var subQ1=sQuery(id+"F0.wireOp",EDGE,"E12.2.5");var subQ2=makeQuery(id+"F0.imprint","INTERSECT",VERTEX,{"derivedFrom":[subQ1,subQ0]});Q7=makeQuery(id+"F0.imprint","IMPRINT",FACE,{"disambiguationData":[TD([[makeQuery(id+"F0.imprint","IMPRINT",EDGE,{"disambiguationData":[TD([[subQ2,-1.0]])],"derivedFrom":subQ1}),-1.0]])]});}
            var Q8;
            Q8=makeQuery(id+"F0.imprint","IMPRINT",FACE,{"disambiguationData":[TD([[makeQuery(id+"F0.imprint","IMPRINT",EDGE,{"derivedFrom":sQuery(id+"F0.wireOp",EDGE,"E3.0.1.9")}),-1.0]])]});
            var Q9;
            {var subQ0=sQuery(id+"F0.wireOp",EDGE,"E3.0.1.5");var subQ1=sQuery(id+"F0.wireOp",EDGE,"E3.0.1.3");var subQ2=makeQuery(id+"F0.imprint","INTERSECT",VERTEX,{"derivedFrom":[subQ1,subQ0]});Q9=makeQuery(id+"F0.imprint","IMPRINT",FACE,{"disambiguationData":[TD([[makeQuery(id+"F0.imprint","IMPRINT",EDGE,{"disambiguationData":[TD([[subQ2,-1.0]])],"derivedFrom":subQ1}),-1.0]])]});}
            var Q10;
            {var subQ0=sQuery(id+"F0.wireOp",EDGE,"E3.0.1.8");var subQ1=sQuery(id+"F0.wireOp",EDGE,"E3.0.1.2");var subQ2=makeQuery(id+"F0.imprint","INTERSECT",VERTEX,{"derivedFrom":[subQ1,subQ0]});Q10=makeQuery(id+"F0.imprint","IMPRINT",FACE,{"disambiguationData":[TD([[makeQuery(id+"F0.imprint","IMPRINT",EDGE,{"disambiguationData":[TD([[subQ2,1.0]])],"derivedFrom":subQ1}),-1.0]])]});}
            var Q11;
            {var subQ0=sQuery(id+"F0.wireOp",EDGE,"E3.0.1.4");var subQ1=sQuery(id+"F0.wireOp",EDGE,"E3.0.1.2");var subQ2=makeQuery(id+"F0.imprint","INTERSECT",VERTEX,{"derivedFrom":[subQ1,subQ0]});Q11=makeQuery(id+"F0.imprint","IMPRINT",FACE,{"disambiguationData":[TD([[makeQuery(id+"F0.imprint","IMPRINT",EDGE,{"disambiguationData":[TD([[subQ2,-1.0]])],"derivedFrom":subQ1}),-1.0]])]});}
            var Q12;
            {var subQ0=sQuery(id+"F0.wireOp",EDGE,"E3.0.1.4");var subQ1=sQuery(id+"F0.wireOp",EDGE,"E3.0.1.3");var subQ2=makeQuery(id+"F0.imprint","INTERSECT",VERTEX,{"derivedFrom":[subQ1,subQ0]});Q12=makeQuery(id+"F0.imprint","IMPRINT",FACE,{"disambiguationData":[TD([[makeQuery(id+"F0.imprint","IMPRINT",EDGE,{"disambiguationData":[TD([[subQ2,-1.0]])],"derivedFrom":subQ1}),-1.0]])]});}
            var Q13;
            {var subQ0=sQuery(id+"F0.wireOp",EDGE,"E3.0.1.7");var subQ1=sQuery(id+"F0.wireOp",EDGE,"E3.0.1.3");var subQ2=makeQuery(id+"F0.imprint","INTERSECT",VERTEX,{"derivedFrom":[subQ1,subQ0]});Q13=makeQuery(id+"F0.imprint","IMPRINT",FACE,{"disambiguationData":[TD([[makeQuery(id+"F0.imprint","IMPRINT",EDGE,{"disambiguationData":[TD([[subQ2,1.0]])],"derivedFrom":subQ1}),-1.0]])]});}
            var Q14;
            {var subQ0=sQuery(id+"F0.wireOp",EDGE,"E3.0.1.5");var subQ1=sQuery(id+"F0.wireOp",EDGE,"E3.0.1.3");var subQ2=makeQuery(id+"F0.imprint","INTERSECT",VERTEX,{"derivedFrom":[subQ1,subQ0]});Q14=makeQuery(id+"F0.imprint","IMPRINT",FACE,{"disambiguationData":[TD([[makeQuery(id+"F0.imprint","IMPRINT",EDGE,{"disambiguationData":[TD([[subQ2,1.0]])],"derivedFrom":subQ1}),-1.0]])]});}
            var Q15;
            Q15=makeQuery(id+"F0.imprint","IMPRINT",FACE,{"disambiguationData":[TD([[makeQuery(id+"F0.imprint","IMPRINT",EDGE,{"derivedFrom":sQuery(id+"F0.wireOp",EDGE,"E1")}),-1.0]])]});
            var Q16;
            {var subQ0=sQuery(id+"F0.wireOp",EDGE,"E2.3");var subQ1=sQuery(id+"F0.wireOp",EDGE,"E2.cCircle");var subQ2=makeQuery(id+"F0.imprint","INTERSECT",VERTEX,{"derivedFrom":[subQ1,subQ0]});Q16=makeQuery(id+"F0.imprint","IMPRINT",FACE,{"disambiguationData":[TD([[makeQuery(id+"F0.imprint","IMPRINT",EDGE,{"disambiguationData":[TD([[subQ2,-1.0]])],"derivedFrom":subQ1}),-1.0]])]});}
            var Q17;
            {var subQ0=sQuery(id+"F0.wireOp",EDGE,"E2.1");var subQ1=sQuery(id+"F0.wireOp",EDGE,"E2.cCircle");var subQ2=makeQuery(id+"F0.imprint","INTERSECT",VERTEX,{"derivedFrom":[subQ1,subQ0]});Q17=makeQuery(id+"F0.imprint","IMPRINT",FACE,{"disambiguationData":[TD([[makeQuery(id+"F0.imprint","IMPRINT",EDGE,{"disambiguationData":[TD([[subQ2,-1.0]])],"derivedFrom":subQ1}),-1.0]])]});}
            var Q18;
            {var subQ0=sQuery(id+"F0.wireOp",EDGE,"E2.5");var subQ1=sQuery(id+"F0.wireOp",EDGE,"E2.cCircle");var subQ2=makeQuery(id+"F0.imprint","INTERSECT",VERTEX,{"derivedFrom":[subQ1,subQ0]});Q18=makeQuery(id+"F0.imprint","IMPRINT",FACE,{"disambiguationData":[TD([[makeQuery(id+"F0.imprint","IMPRINT",EDGE,{"disambiguationData":[TD([[subQ2,1.0]])],"derivedFrom":subQ1}),-1.0]])]});}
            var Q19;
            {var subQ0=sQuery(id+"F0.wireOp",EDGE,"E2.4");var subQ1=sQuery(id+"F0.wireOp",EDGE,"E2.cCircle");var subQ2=makeQuery(id+"F0.imprint","INTERSECT",VERTEX,{"derivedFrom":[subQ1,subQ0]});Q19=makeQuery(id+"F0.imprint","IMPRINT",FACE,{"disambiguationData":[TD([[makeQuery(id+"F0.imprint","IMPRINT",EDGE,{"disambiguationData":[TD([[subQ2,1.0]])],"derivedFrom":subQ1}),-1.0]])]});}
            var Q20;
            {var subQ0=sQuery(id+"F0.wireOp",EDGE,"E2.4");var subQ1=sQuery(id+"F0.wireOp",EDGE,"E2.cCircle");var subQ2=makeQuery(id+"F0.imprint","INTERSECT",VERTEX,{"derivedFrom":[subQ1,subQ0]});Q20=makeQuery(id+"F0.imprint","IMPRINT",FACE,{"disambiguationData":[TD([[makeQuery(id+"F0.imprint","IMPRINT",EDGE,{"disambiguationData":[TD([[subQ2,-1.0]])],"derivedFrom":subQ1}),-1.0]])]});}
            var Q21;
            {var subQ0=sQuery(id+"F0.wireOp",EDGE,"E2.2");var subQ1=sQuery(id+"F0.wireOp",EDGE,"E2.cCircle");var subQ2=makeQuery(id+"F0.imprint","INTERSECT",VERTEX,{"derivedFrom":[subQ1,subQ0]});Q21=makeQuery(id+"F0.imprint","IMPRINT",FACE,{"disambiguationData":[TD([[makeQuery(id+"F0.imprint","IMPRINT",EDGE,{"disambiguationData":[TD([[subQ2,-1.0]])],"derivedFrom":subQ1}),-1.0]])]});}
            var Q22;
            Q22=makeQuery(id+"F0.imprint","IMPRINT",FACE,{"disambiguationData":[TD([[makeQuery(id+"F0.imprint","IMPRINT",EDGE,{"derivedFrom":sQuery(id+"F0.wireOp",EDGE,"E12.1.6")}),-1.0]])]});
            var Q23;
            {var subQ0=sQuery(id+"F0.wireOp",EDGE,"E12.1.10");var subQ1=sQuery(id+"F0.wireOp",EDGE,"E12.1.5");var subQ2=makeQuery(id+"F0.imprint","INTERSECT",VERTEX,{"derivedFrom":[subQ1,subQ0]});Q23=makeQuery(id+"F0.imprint","IMPRINT",FACE,{"disambiguationData":[TD([[makeQuery(id+"F0.imprint","IMPRINT",EDGE,{"disambiguationData":[TD([[subQ2,1.0]])],"derivedFrom":subQ1}),-1.0]])]});}
            var Q24;
            {var subQ0=sQuery(id+"F0.wireOp",EDGE,"E12.1.10");var subQ1=sQuery(id+"F0.wireOp",EDGE,"E12.1.5");var subQ2=makeQuery(id+"F0.imprint","INTERSECT",VERTEX,{"derivedFrom":[subQ1,subQ0]});Q24=makeQuery(id+"F0.imprint","IMPRINT",FACE,{"disambiguationData":[TD([[makeQuery(id+"F0.imprint","IMPRINT",EDGE,{"disambiguationData":[TD([[subQ2,-1.0]])],"derivedFrom":subQ1}),-1.0]])]});}
            var Q25;
            {var subQ0=sQuery(id+"F0.wireOp",EDGE,"E12.1.12");var subQ1=sQuery(id+"F0.wireOp",EDGE,"E12.1.5");var subQ2=makeQuery(id+"F0.imprint","INTERSECT",VERTEX,{"derivedFrom":[subQ1,subQ0]});Q25=makeQuery(id+"F0.imprint","IMPRINT",FACE,{"disambiguationData":[TD([[makeQuery(id+"F0.imprint","IMPRINT",EDGE,{"disambiguationData":[TD([[subQ2,-1.0]])],"derivedFrom":subQ1}),-1.0]])]});}
            var Q26;
            {var subQ0=sQuery(id+"F0.wireOp",EDGE,"E12.1.11");var subQ1=sQuery(id+"F0.wireOp",EDGE,"E12.1.5");var subQ2=makeQuery(id+"F0.imprint","INTERSECT",VERTEX,{"derivedFrom":[subQ1,subQ0]});Q26=makeQuery(id+"F0.imprint","IMPRINT",FACE,{"disambiguationData":[TD([[makeQuery(id+"F0.imprint","IMPRINT",EDGE,{"disambiguationData":[TD([[subQ2,-1.0]])],"derivedFrom":subQ1}),-1.0]])]});}
            var Q27;
            {var subQ0=sQuery(id+"F0.wireOp",EDGE,"E12.1.15");var subQ1=sQuery(id+"F0.wireOp",EDGE,"E12.1.5");var subQ2=makeQuery(id+"F0.imprint","INTERSECT",VERTEX,{"derivedFrom":[subQ1,subQ0]});Q27=makeQuery(id+"F0.imprint","IMPRINT",FACE,{"disambiguationData":[TD([[makeQuery(id+"F0.imprint","IMPRINT",EDGE,{"disambiguationData":[TD([[subQ2,-1.0]])],"derivedFrom":subQ1}),-1.0]])]});}
            var Q28;
            {var subQ0=sQuery(id+"F0.wireOp",EDGE,"E12.1.13");var subQ1=sQuery(id+"F0.wireOp",EDGE,"E12.1.5");var subQ2=makeQuery(id+"F0.imprint","INTERSECT",VERTEX,{"derivedFrom":[subQ1,subQ0]});Q28=makeQuery(id+"F0.imprint","IMPRINT",FACE,{"disambiguationData":[TD([[makeQuery(id+"F0.imprint","IMPRINT",EDGE,{"disambiguationData":[TD([[subQ2,1.0]])],"derivedFrom":subQ1}),-1.0]])]});}
            extrude(context, id + "F4", {"entities" : qUnion([Q0, Q1, Q2, Q3, Q4, Q5, Q6, Q7, Q8, Q9, Q10, Q11, Q12, Q13, Q14, Q15, Q16, Q17, Q18, Q19, Q20, Q21, Q22, Q23, Q24, Q25, Q26, Q27, Q28]), "depth" : 4 * mm, "offsetDistance" : 25 * mm});
        }
        {
            var Q0;
            Q0=makeQuery(id+"F0.imprint","IMPRINT",FACE,{"disambiguationData":[TD([[makeQuery(id+"F0.imprint","IMPRINT",EDGE,{"derivedFrom":sQuery(id+"F0.wireOp",EDGE,"E12.1.6")}),-1.0]])]});
            var Q1;
            Q1=makeQuery(id+"F0.imprint","IMPRINT",FACE,{"disambiguationData":[TD([[makeQuery(id+"F0.imprint","IMPRINT",EDGE,{"derivedFrom":sQuery(id+"F0.wireOp",EDGE,"E3.0.1.9")}),-1.0]])]});
            var Q2;
            Q2=makeQuery(id+"F0.imprint","IMPRINT",FACE,{"disambiguationData":[TD([[makeQuery(id+"F0.imprint","IMPRINT",EDGE,{"derivedFrom":sQuery(id+"F0.wireOp",EDGE,"E1")}),-1.0]])]});
            var Q3;
            Q3=makeQuery(id+"F0.imprint","IMPRINT",FACE,{"disambiguationData":[TD([[makeQuery(id+"F0.imprint","IMPRINT",EDGE,{"derivedFrom":sQuery(id+"F0.wireOp",EDGE,"E12.2.6")}),-1.0]])]});
            extrude(context, id + "F5", {"entities" : qUnion([Q0, Q1, Q2, Q3]), "operationType" : NewBodyOperationType.REMOVE, "depth" : 2 * mm, "offsetDistance" : 25 * mm});
        }
        {
            var Q0;
            Q0=makeQuery(id+"F4.opExtrude","CAP_EDGE",EDGE,{"disambiguationData":[OSD([sQuery(id+"F0.wireOp",EDGE,"E8")])],"isStart":true});
            fillet(context, id + "F6", {"entities" : qUnion([Q0]), "radius" : 1 * mm, "tangentPropagation" : true, "allowEdgeOverflow" : false});
        }
    });
